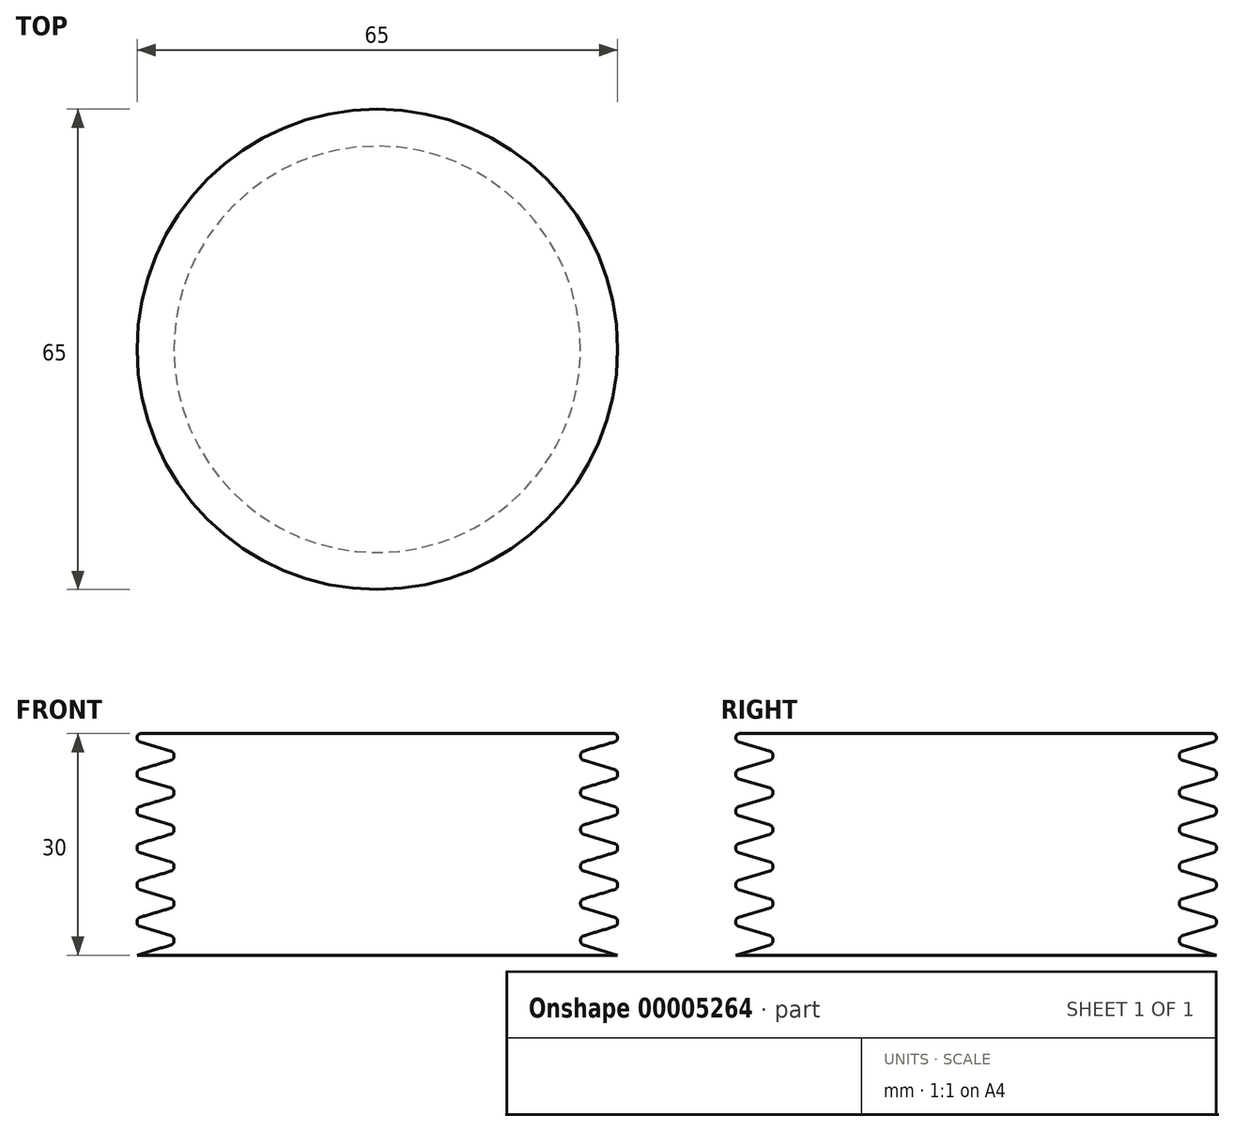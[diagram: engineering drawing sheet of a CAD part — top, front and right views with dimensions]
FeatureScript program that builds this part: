
annotation { "Feature Type Name" : "Feature", "Feature Type Description" : "" }
export const myFeature = defineFeature(function(context is Context, id is Id, definition is map)
    precondition{}
    {
        {
            var Q0;
            Q0=qCreatedBy(makeId("Front.planeOp"),FACE);
            var sketch = newSketch(context, id + "F0", { "sketchPlane" : qUnion([Q0])});
            skLineSegment(sketch, "E0", {"start": v(-32.5, 0) * mm, "end": v(-27.5, 1.5) * mm});
            skLineSegment(sketch, "E1", {"start": v(-27.5, 1.5) * mm, "end": v(-27.5, 2.5) * mm});
            skLineSegment(sketch, "E2", {"start": v(-27.5, 2.5) * mm, "end": v(-32.5, 4) * mm});
            skLineSegment(sketch, "E3", {"start": v(-32.5, 4) * mm, "end": v(-32.5, 5) * mm});
            skLineSegment(sketch, "E4", {"start": v(-32.5, 0) * mm, "end": v(0, 0) * mm});
            skLineSegment(sketch, "E5", {"start": v(0, 0) * mm, "end": v(0, 30) * mm});
            skLineSegment(sketch, "E6", {"start": v(-32.5, 4) * mm, "end": v(-32.5, 0) * mm, "construction": true});
            skPoint(sketch, "E7", {"position": v(-32.5, 2) * mm});
            skPoint(sketch, "E8", {"position": v(-27.5, 2) * mm});
            skLineSegment(sketch, "E9.0.1.0", {"start": v(-32.5, 9) * mm, "end": v(-32.5, 5) * mm, "construction": true});
            skLineSegment(sketch, "E9.0.1.1", {"start": v(-27.5, 7.5) * mm, "end": v(-32.5, 9) * mm});
            skLineSegment(sketch, "E9.0.1.2", {"start": v(-32.5, 5) * mm, "end": v(-27.5, 6.5) * mm});
            skPoint(sketch, "E9.0.1.3", {"position": v(-27.5, 7) * mm});
            skPoint(sketch, "E9.0.1.4", {"position": v(-32.5, 7) * mm});
            skLineSegment(sketch, "E9.0.1.5", {"start": v(-32.5, 9) * mm, "end": v(-32.5, 10) * mm});
            skLineSegment(sketch, "E9.0.1.6", {"start": v(-27.5, 6.5) * mm, "end": v(-27.5, 7.5) * mm});
            skLineSegment(sketch, "E9.0.2.0", {"start": v(-32.5, 14) * mm, "end": v(-32.5, 10) * mm, "construction": true});
            skLineSegment(sketch, "E9.0.2.1", {"start": v(-27.5, 12.5) * mm, "end": v(-32.5, 14) * mm});
            skLineSegment(sketch, "E9.0.2.2", {"start": v(-32.5, 10) * mm, "end": v(-27.5, 11.5) * mm});
            skPoint(sketch, "E9.0.2.3", {"position": v(-27.5, 12) * mm});
            skPoint(sketch, "E9.0.2.4", {"position": v(-32.5, 12) * mm});
            skLineSegment(sketch, "E9.0.2.5", {"start": v(-32.5, 14) * mm, "end": v(-32.5, 15) * mm});
            skLineSegment(sketch, "E9.0.2.6", {"start": v(-27.5, 11.5) * mm, "end": v(-27.5, 12.5) * mm});
            skLineSegment(sketch, "E9.0.3.0", {"start": v(-32.5, 19) * mm, "end": v(-32.5, 15) * mm, "construction": true});
            skLineSegment(sketch, "E9.0.3.1", {"start": v(-27.5, 17.5) * mm, "end": v(-32.5, 19) * mm});
            skLineSegment(sketch, "E9.0.3.2", {"start": v(-32.5, 15) * mm, "end": v(-27.5, 16.5) * mm});
            skPoint(sketch, "E9.0.3.3", {"position": v(-27.5, 17) * mm});
            skPoint(sketch, "E9.0.3.4", {"position": v(-32.5, 17) * mm});
            skLineSegment(sketch, "E9.0.3.5", {"start": v(-32.5, 19) * mm, "end": v(-32.5, 20) * mm});
            skLineSegment(sketch, "E9.0.3.6", {"start": v(-27.5, 16.5) * mm, "end": v(-27.5, 17.5) * mm});
            skLineSegment(sketch, "E9.0.4.0", {"start": v(-32.5, 24) * mm, "end": v(-32.5, 20) * mm, "construction": true});
            skLineSegment(sketch, "E9.0.4.1", {"start": v(-27.5, 22.5) * mm, "end": v(-32.5, 24) * mm});
            skLineSegment(sketch, "E9.0.4.2", {"start": v(-32.5, 20) * mm, "end": v(-27.5, 21.5) * mm});
            skPoint(sketch, "E9.0.4.3", {"position": v(-27.5, 22) * mm});
            skPoint(sketch, "E9.0.4.4", {"position": v(-32.5, 22) * mm});
            skLineSegment(sketch, "E9.0.4.5", {"start": v(-32.5, 24) * mm, "end": v(-32.5, 25) * mm});
            skLineSegment(sketch, "E9.0.4.6", {"start": v(-27.5, 21.5) * mm, "end": v(-27.5, 22.5) * mm});
            skLineSegment(sketch, "E9.0.5.0", {"start": v(-32.5, 29) * mm, "end": v(-32.5, 25) * mm, "construction": true});
            skLineSegment(sketch, "E9.0.5.1", {"start": v(-27.5, 27.5) * mm, "end": v(-32.5, 29) * mm});
            skLineSegment(sketch, "E9.0.5.2", {"start": v(-32.5, 25) * mm, "end": v(-27.5, 26.5) * mm});
            skPoint(sketch, "E9.0.5.3", {"position": v(-27.5, 27) * mm});
            skPoint(sketch, "E9.0.5.4", {"position": v(-32.5, 27) * mm});
            skLineSegment(sketch, "E9.0.5.5", {"start": v(-32.5, 29) * mm, "end": v(-32.5, 30) * mm});
            skLineSegment(sketch, "E9.0.5.6", {"start": v(-27.5, 26.5) * mm, "end": v(-27.5, 27.5) * mm});
            skLineSegment(sketch, "E9.direction1", {"start": v(-37, 0) * mm, "end": v(-32.5, 0) * mm, "construction": true});
            skLineSegment(sketch, "E9.direction2", {"start": v(-32.5, 0) * mm, "end": v(-32.5, 5) * mm, "construction": true});
            skLineSegment(sketch, "E10", {"start": v(-32.5, 30) * mm, "end": v(0, 30) * mm});
            skSolve(sketch);
        }
        {
            var Q0;
            Q0=makeQuery(id+"F0.imprint","IMPRINT",FACE,{"disambiguationData":[TD([[makeQuery(id+"F0.imprint","IMPRINT",EDGE,{"derivedFrom":sQuery(id+"F0.wireOp",EDGE,"E0")}),-1.0]])]});
            var Q1;
            Q1=sQuery(id+"F0.wireOp",EDGE,"E5");
            revolve(context, id + "F1", {"entities" : qUnion([Q0]), "axis" : qUnion([Q1]), "revolveType" : RevolveType.FULL});
        }
        {
            var Q0;
            Q0=makeQuery(id+"F1.opRevolve","SWEPT_EDGE",EDGE,{"disambiguationData":[OSD([sQuery(id+"F0.wireOp",EDGE,"E9.0.5.5"),sQuery(id+"F0.wireOp",EDGE,"E10")])]});
            var Q1;
            Q1=makeQuery(id+"F1.opRevolve","SWEPT_EDGE",EDGE,{"disambiguationData":[OSD([sQuery(id+"F0.wireOp",EDGE,"E9.0.5.1"),sQuery(id+"F0.wireOp",EDGE,"E9.0.5.5")])]});
            var Q2;
            Q2=makeQuery(id+"F1.opRevolve","SWEPT_EDGE",EDGE,{"disambiguationData":[OSD([sQuery(id+"F0.wireOp",EDGE,"E9.0.5.1"),sQuery(id+"F0.wireOp",EDGE,"E9.0.5.6")])]});
            var Q3;
            Q3=makeQuery(id+"F1.opRevolve","SWEPT_EDGE",EDGE,{"disambiguationData":[OSD([sQuery(id+"F0.wireOp",EDGE,"E9.0.5.2"),sQuery(id+"F0.wireOp",EDGE,"E9.0.5.6")])]});
            var Q4;
            Q4=makeQuery(id+"F1.opRevolve","SWEPT_EDGE",EDGE,{"disambiguationData":[OSD([sQuery(id+"F0.wireOp",EDGE,"E9.0.4.5"),sQuery(id+"F0.wireOp",EDGE,"E9.0.5.2")])]});
            var Q5;
            Q5=makeQuery(id+"F1.opRevolve","SWEPT_EDGE",EDGE,{"disambiguationData":[OSD([sQuery(id+"F0.wireOp",EDGE,"E9.0.4.1"),sQuery(id+"F0.wireOp",EDGE,"E9.0.4.5")])]});
            var Q6;
            Q6=makeQuery(id+"F1.opRevolve","SWEPT_EDGE",EDGE,{"disambiguationData":[OSD([sQuery(id+"F0.wireOp",EDGE,"E9.0.4.1"),sQuery(id+"F0.wireOp",EDGE,"E9.0.4.6")])]});
            var Q7;
            Q7=makeQuery(id+"F1.opRevolve","SWEPT_EDGE",EDGE,{"disambiguationData":[OSD([sQuery(id+"F0.wireOp",EDGE,"E9.0.4.2"),sQuery(id+"F0.wireOp",EDGE,"E9.0.4.6")])]});
            var Q8;
            Q8=makeQuery(id+"F1.opRevolve","SWEPT_EDGE",EDGE,{"disambiguationData":[OSD([sQuery(id+"F0.wireOp",EDGE,"E9.0.3.5"),sQuery(id+"F0.wireOp",EDGE,"E9.0.4.2")])]});
            var Q9;
            Q9=makeQuery(id+"F1.opRevolve","SWEPT_EDGE",EDGE,{"disambiguationData":[OSD([sQuery(id+"F0.wireOp",EDGE,"E9.0.3.1"),sQuery(id+"F0.wireOp",EDGE,"E9.0.3.5")])]});
            var Q10;
            Q10=makeQuery(id+"F1.opRevolve","SWEPT_EDGE",EDGE,{"disambiguationData":[OSD([sQuery(id+"F0.wireOp",EDGE,"E9.0.3.1"),sQuery(id+"F0.wireOp",EDGE,"E9.0.3.6")])]});
            var Q11;
            Q11=makeQuery(id+"F1.opRevolve","SWEPT_EDGE",EDGE,{"disambiguationData":[OSD([sQuery(id+"F0.wireOp",EDGE,"E9.0.3.2"),sQuery(id+"F0.wireOp",EDGE,"E9.0.3.6")])]});
            var Q12;
            Q12=makeQuery(id+"F1.opRevolve","SWEPT_EDGE",EDGE,{"disambiguationData":[OSD([sQuery(id+"F0.wireOp",EDGE,"E9.0.2.5"),sQuery(id+"F0.wireOp",EDGE,"E9.0.3.2")])]});
            var Q13;
            Q13=makeQuery(id+"F1.opRevolve","SWEPT_EDGE",EDGE,{"disambiguationData":[OSD([sQuery(id+"F0.wireOp",EDGE,"E9.0.2.1"),sQuery(id+"F0.wireOp",EDGE,"E9.0.2.5")])]});
            var Q14;
            Q14=makeQuery(id+"F1.opRevolve","SWEPT_FACE",FACE,{"disambiguationData":[OSD([sQuery(id+"F0.wireOp",EDGE,"E9.0.2.1")])]});
            var Q15;
            Q15=makeQuery(id+"F1.opRevolve","SWEPT_EDGE",EDGE,{"disambiguationData":[OSD([sQuery(id+"F0.wireOp",EDGE,"E9.0.2.1"),sQuery(id+"F0.wireOp",EDGE,"E9.0.2.6")])]});
            var Q16;
            Q16=makeQuery(id+"F1.opRevolve","SWEPT_EDGE",EDGE,{"disambiguationData":[OSD([sQuery(id+"F0.wireOp",EDGE,"E9.0.2.2"),sQuery(id+"F0.wireOp",EDGE,"E9.0.2.6")])]});
            var Q17;
            Q17=makeQuery(id+"F1.opRevolve","SWEPT_FACE",FACE,{"disambiguationData":[OSD([sQuery(id+"F0.wireOp",EDGE,"E9.0.2.2")])]});
            var Q18;
            Q18=makeQuery(id+"F1.opRevolve","SWEPT_EDGE",EDGE,{"disambiguationData":[OSD([sQuery(id+"F0.wireOp",EDGE,"E9.0.1.1"),sQuery(id+"F0.wireOp",EDGE,"E9.0.1.5")])]});
            var Q19;
            Q19=makeQuery(id+"F1.opRevolve","SWEPT_EDGE",EDGE,{"disambiguationData":[OSD([sQuery(id+"F0.wireOp",EDGE,"E9.0.1.5"),sQuery(id+"F0.wireOp",EDGE,"E9.0.2.2")])]});
            var Q20;
            Q20=makeQuery(id+"F1.opRevolve","SWEPT_EDGE",EDGE,{"disambiguationData":[OSD([sQuery(id+"F0.wireOp",EDGE,"E9.0.1.1"),sQuery(id+"F0.wireOp",EDGE,"E9.0.1.6")])]});
            var Q21;
            Q21=makeQuery(id+"F1.opRevolve","SWEPT_EDGE",EDGE,{"disambiguationData":[OSD([sQuery(id+"F0.wireOp",EDGE,"E9.0.1.2"),sQuery(id+"F0.wireOp",EDGE,"E9.0.1.6")])]});
            var Q22;
            Q22=makeQuery(id+"F1.opRevolve","SWEPT_EDGE",EDGE,{"disambiguationData":[OSD([sQuery(id+"F0.wireOp",EDGE,"E3"),sQuery(id+"F0.wireOp",EDGE,"E9.0.1.2")])]});
            var Q23;
            Q23=makeQuery(id+"F1.opRevolve","SWEPT_EDGE",EDGE,{"disambiguationData":[OSD([sQuery(id+"F0.wireOp",EDGE,"E2"),sQuery(id+"F0.wireOp",EDGE,"E3")])]});
            var Q24;
            Q24=makeQuery(id+"F1.opRevolve","SWEPT_EDGE",EDGE,{"disambiguationData":[OSD([sQuery(id+"F0.wireOp",EDGE,"E1"),sQuery(id+"F0.wireOp",EDGE,"E2")])]});
            var Q25;
            Q25=makeQuery(id+"F1.opRevolve","SWEPT_EDGE",EDGE,{"disambiguationData":[OSD([sQuery(id+"F0.wireOp",EDGE,"E0"),sQuery(id+"F0.wireOp",EDGE,"E1")])]});
            fillet(context, id + "F2", {"entities" : qUnion([Q0, Q1, Q2, Q3, Q4, Q5, Q6, Q7, Q8, Q9, Q10, Q11, Q12, Q13, Q14, Q15, Q16, Q17, Q18, Q19, Q20, Q21, Q22, Q23, Q24, Q25]), "radius" : 0.55 * mm, "tangentPropagation" : true, "allowEdgeOverflow" : false});
        }
    });
